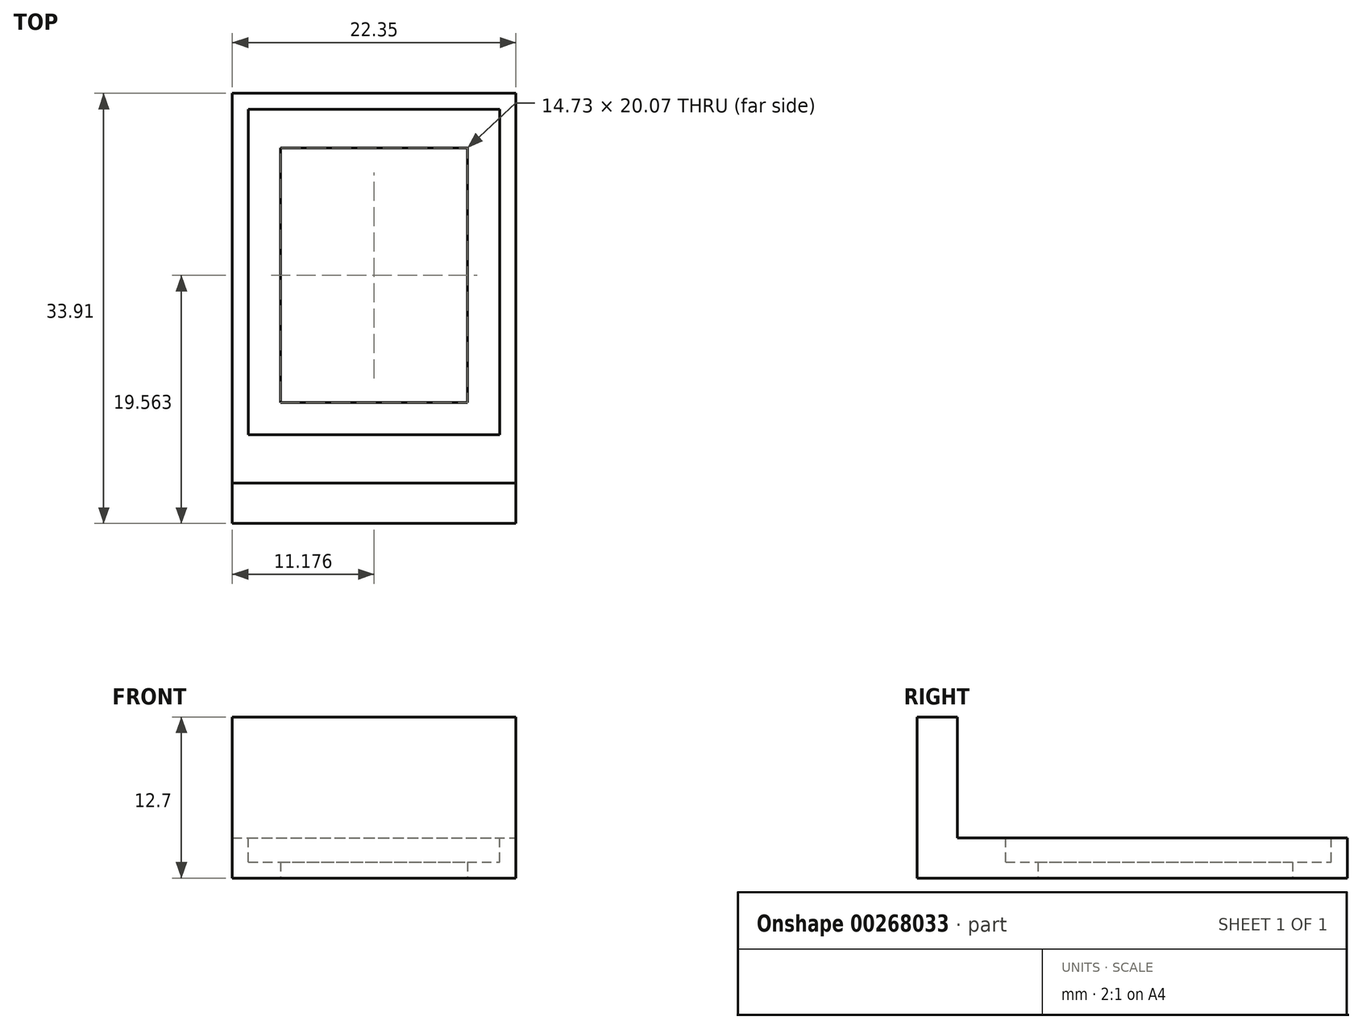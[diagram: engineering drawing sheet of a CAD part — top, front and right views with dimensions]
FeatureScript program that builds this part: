
annotation { "Feature Type Name" : "Feature", "Feature Type Description" : "" }
export const myFeature = defineFeature(function(context is Context, id is Id, definition is map)
    precondition{}
    {
        {
            var Q0;
            Q0=qCreatedBy(makeId("Top.planeOp"),FACE);
            var sketch = newSketch(context, id + "F0", { "sketchPlane" : qUnion([Q0])});
            skLineSegment(sketch, "E0.bottom", {"start": v(0, 0) * mm, "end": v(22.35, 0) * mm});
            skLineSegment(sketch, "E0.top", {"start": v(0, 30.73) * mm, "end": v(22.35, 30.73) * mm});
            skLineSegment(sketch, "E0.left", {"start": v(0, 0) * mm, "end": v(0, 30.73) * mm});
            skLineSegment(sketch, "E0.right", {"start": v(22.35, 0) * mm, "end": v(22.35, 30.73) * mm});
            skLineSegment(sketch, "E1.bottom", {"start": v(3.8, 6.35) * mm, "end": v(18.54, 6.35) * mm});
            skLineSegment(sketch, "E1.top", {"start": v(3.8, 26.42) * mm, "end": v(18.54, 26.42) * mm});
            skLineSegment(sketch, "E1.left", {"start": v(3.8, 6.35) * mm, "end": v(3.8, 26.42) * mm});
            skLineSegment(sketch, "E1.right", {"start": v(18.54, 6.35) * mm, "end": v(18.54, 26.42) * mm});
            skLineSegment(sketch, "E2.bottom", {"start": v(0, 0) * mm, "end": v(3.81, 0) * mm, "construction": true});
            skLineSegment(sketch, "E2.top", {"start": v(0, 6.35) * mm, "end": v(3.8, 6.35) * mm, "construction": true});
            skLineSegment(sketch, "E2.left", {"start": v(0, 0) * mm, "end": v(0, 6.35) * mm, "construction": true});
            skLineSegment(sketch, "E2.right", {"start": v(3.81, 0) * mm, "end": v(3.8, 6.35) * mm, "construction": true});
            skLineSegment(sketch, "E3.top", {"start": v(0, -3.18) * mm, "end": v(22.35, -3.18) * mm});
            skLineSegment(sketch, "E3.left", {"start": v(0, 0) * mm, "end": v(0, -3.18) * mm});
            skLineSegment(sketch, "E3.right", {"start": v(22.35, 0) * mm, "end": v(22.35, -3.18) * mm});
            skSolve(sketch);
        }
        {
            var Q0;
            Q0=makeQuery(id+"F0.imprint","IMPRINT",FACE,{"disambiguationData":[TD([[makeQuery(id+"F0.imprint","IMPRINT",EDGE,{"derivedFrom":sQuery(id+"F0.wireOp",EDGE,"E0.top")}),-1.0]])]});
            extrude(context, id + "F1", {"entities" : qUnion([Q0]), "depth" : 3.17 * mm});
        }
        {
            var Q0;
            Q0=makeQuery(id+"F1.opExtrude","CAP_FACE",FACE,{"disambiguationData":[OSD([sQuery(id+"F0.wireOp",EDGE,"E0.bottom"),sQuery(id+"F0.wireOp",EDGE,"E0.top"),sQuery(id+"F0.wireOp",EDGE,"E0.left"),sQuery(id+"F0.wireOp",EDGE,"E0.right"),sQuery(id+"F0.wireOp",EDGE,"E1.bottom"),sQuery(id+"F0.wireOp",EDGE,"E1.top"),sQuery(id+"F0.wireOp",EDGE,"E1.left"),sQuery(id+"F0.wireOp",EDGE,"E1.right")])],"isStart":false});
            var sketch = newSketch(context, id + "F2", { "sketchPlane" : qUnion([Q0])});
            skLineSegment(sketch, "E4.bottom", {"start": v(1.27, 3.81) * mm, "end": v(21.08, 3.81) * mm});
            skLineSegment(sketch, "E4.top", {"start": v(1.27, 29.46) * mm, "end": v(21.08, 29.46) * mm});
            skLineSegment(sketch, "E4.left", {"start": v(1.27, 3.81) * mm, "end": v(1.27, 29.46) * mm});
            skLineSegment(sketch, "E4.right", {"start": v(21.08, 3.81) * mm, "end": v(21.08, 29.46) * mm});
            skLineSegment(sketch, "E5.bottom", {"start": v(3.8, 6.35) * mm, "end": v(1.27, 6.35) * mm, "construction": true});
            skLineSegment(sketch, "E5.top", {"start": v(3.81, 3.81) * mm, "end": v(1.27, 3.81) * mm, "construction": true});
            skLineSegment(sketch, "E5.left", {"start": v(3.8, 6.35) * mm, "end": v(3.81, 3.81) * mm, "construction": true});
            skLineSegment(sketch, "E5.right", {"start": v(1.27, 6.35) * mm, "end": v(1.27, 3.81) * mm, "construction": true});
            skSolve(sketch);
        }
        {
            var Q0;
            Q0=makeQuery(id+"F2.imprint","IMPRINT",FACE,{"disambiguationData":[TD([[makeQuery(id+"F2.imprint","IMPRINT",EDGE,{"derivedFrom":sQuery(id+"F2.wireOp",EDGE,"E4.bottom")}),1.0]])]});
            extrude(context, id + "F3", {"entities" : qUnion([Q0]), "operationType" : NewBodyOperationType.REMOVE, "oppositeDirection" : true, "depth" : 1.9 * mm});
        }
        {
            var Q0;
            Q0=makeQuery(id+"F0.imprint","IMPRINT",FACE,{"disambiguationData":[TD([[makeQuery(id+"F0.imprint","IMPRINT",EDGE,{"derivedFrom":sQuery(id+"F0.wireOp",EDGE,"E0.bottom")}),-1.0]])]});
            extrude(context, id + "F4", {"entities" : qUnion([Q0]), "operationType" : NewBodyOperationType.ADD, "depth" : 12.7 * mm});
        }
    });
